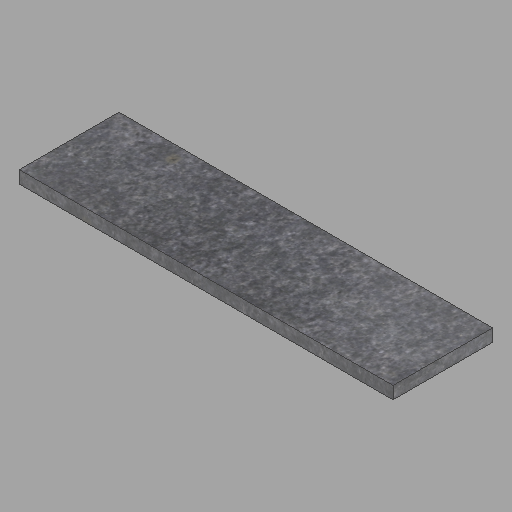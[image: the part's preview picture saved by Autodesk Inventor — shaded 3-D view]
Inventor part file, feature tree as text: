
AUTODESK INVENTOR PART (.ipt)
format: ipt  version: 2023 (Build 270158000, 158)  size: 192,000 bytes
history: native  units: in
note: dims shown in document units (in); Inventor stores cm internally (conversion verified against a paired STEP export)
features: other x1, extrude x1, sketch x1
ambient origin geometry x8: Origin, YZ Plane, XZ Plane, XY Plane, X Axis, Y Axis, Z Axis, Center Point
bodies: Solid1 (feature_tree)
feature tree (3):
  other  "2x16x60-12"
  extrude  "Extrusion1"  Depth=16.0in
  sketch  "Sketch1"  dims[d0=2.0in d1=16.0in d2=60.0in d3=0.0in]
